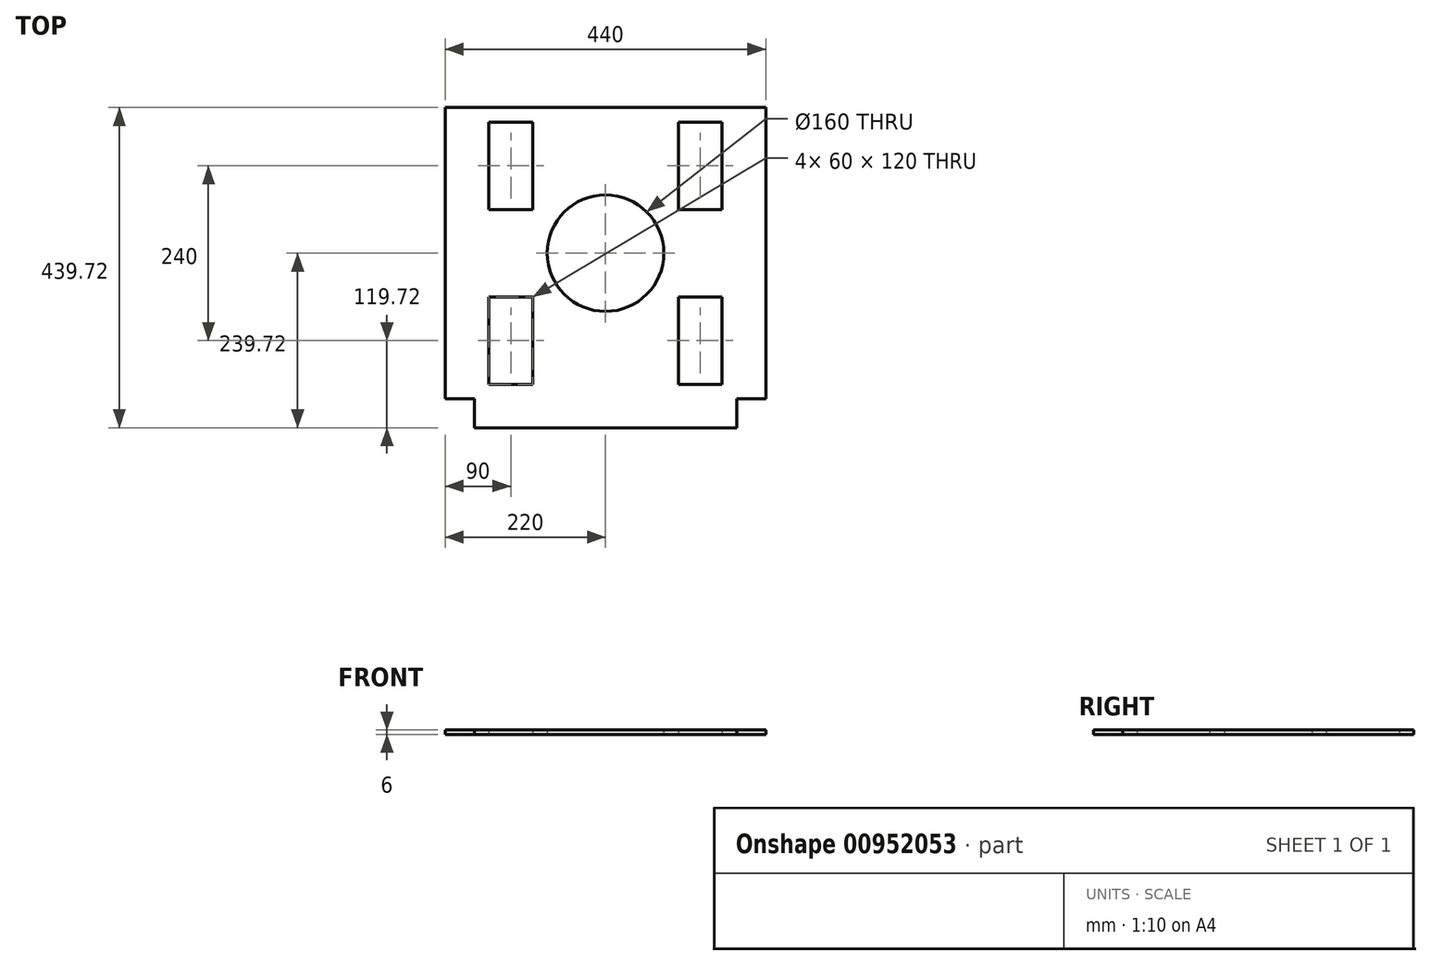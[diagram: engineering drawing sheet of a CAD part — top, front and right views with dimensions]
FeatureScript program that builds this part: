
annotation { "Feature Type Name" : "Feature", "Feature Type Description" : "" }
export const myFeature = defineFeature(function(context is Context, id is Id, definition is map)
    precondition{}
    {
        {
            var Q0;
            Q0=qCreatedBy(makeId("Top.planeOp"),FACE);
            var sketch = newSketch(context, id + "F0", { "sketchPlane" : qUnion([Q0])});
            skLineSegment(sketch, "E0.bottom", {"start": v(180, -200) * mm, "end": v(-180, -200) * mm});
            skLineSegment(sketch, "E0.top", {"start": v(180, 200) * mm, "end": v(-180, 200) * mm});
            skLineSegment(sketch, "E0.left", {"start": v(180, -200) * mm, "end": v(180, 200) * mm});
            skLineSegment(sketch, "E0.right", {"start": v(-180, -200) * mm, "end": v(-180, 200) * mm});
            skPoint(sketch, "E0.middle", {"position": v(0, 0) * mm});
            skLineSegment(sketch, "E1.bottom", {"start": v(-160, 180) * mm, "end": v(-100, 180) * mm});
            skLineSegment(sketch, "E1.top", {"start": v(-160, 60) * mm, "end": v(-100, 60) * mm});
            skLineSegment(sketch, "E1.left", {"start": v(-160, 180) * mm, "end": v(-160, 60) * mm});
            skLineSegment(sketch, "E1.right", {"start": v(-100, 180) * mm, "end": v(-100, 60) * mm});
            skLineSegment(sketch, "E2.MirrorCS", {"start": v(100, 180) * mm, "end": v(100, 60) * mm});
            skLineSegment(sketch, "E3.MirrorCS", {"start": v(160, 180) * mm, "end": v(100, 180) * mm});
            skLineSegment(sketch, "E4.MirrorCS", {"start": v(160, 180) * mm, "end": v(160, 60) * mm});
            skLineSegment(sketch, "E5.MirrorCS", {"start": v(160, 60) * mm, "end": v(100, 60) * mm});
            skLineSegment(sketch, "E6.MirrorCS", {"start": v(-160, -60) * mm, "end": v(-100, -60) * mm});
            skLineSegment(sketch, "E7.MirrorCS", {"start": v(-100, -180) * mm, "end": v(-100, -60) * mm});
            skLineSegment(sketch, "E8.MirrorCS", {"start": v(-160, -180) * mm, "end": v(-160, -60) * mm});
            skLineSegment(sketch, "E9.MirrorCS", {"start": v(-160, -180) * mm, "end": v(-100, -180) * mm});
            skLineSegment(sketch, "E10.MirrorCS", {"start": v(160, -60) * mm, "end": v(100, -60) * mm});
            skLineSegment(sketch, "E11.MirrorCS", {"start": v(100, -180) * mm, "end": v(100, -60) * mm});
            skLineSegment(sketch, "E12.MirrorCS", {"start": v(160, -180) * mm, "end": v(160, -60) * mm});
            skLineSegment(sketch, "E13.MirrorCS", {"start": v(160, -180) * mm, "end": v(100, -180) * mm});
            skLineSegment(sketch, "E14.bottom", {"start": v(-180, 200) * mm, "end": v(180, 200) * mm});
            skLineSegment(sketch, "E14.top", {"start": v(-180, 240) * mm, "end": v(180, 240) * mm});
            skLineSegment(sketch, "E14.left", {"start": v(-180, 200) * mm, "end": v(-180, 240) * mm});
            skLineSegment(sketch, "E14.right", {"start": v(180, 200) * mm, "end": v(180, 240) * mm});
            skLineSegment(sketch, "E15.bottom", {"start": v(180, 200) * mm, "end": v(220, 200) * mm});
            skLineSegment(sketch, "E15.top", {"start": v(180, -199.72) * mm, "end": v(220, -199.72) * mm});
            skLineSegment(sketch, "E15.left", {"start": v(180, 200) * mm, "end": v(180, -199.72) * mm});
            skLineSegment(sketch, "E15.right", {"start": v(220, 200) * mm, "end": v(220, -199.72) * mm});
            skLineSegment(sketch, "E16.bottom", {"start": v(180, -199.72) * mm, "end": v(-180, -199.72) * mm});
            skLineSegment(sketch, "E16.top", {"start": v(180, -239.72) * mm, "end": v(-180, -239.72) * mm});
            skLineSegment(sketch, "E16.left", {"start": v(180, -199.72) * mm, "end": v(180, -239.72) * mm});
            skLineSegment(sketch, "E16.right", {"start": v(-180, -199.72) * mm, "end": v(-180, -239.72) * mm});
            skLineSegment(sketch, "E17.bottom", {"start": v(-180, -199.72) * mm, "end": v(-220, -199.72) * mm});
            skLineSegment(sketch, "E17.top", {"start": v(-180, 200) * mm, "end": v(-220, 200) * mm});
            skLineSegment(sketch, "E17.left", {"start": v(-180, -199.72) * mm, "end": v(-180, 200) * mm});
            skLineSegment(sketch, "E17.right", {"start": v(-220, -199.72) * mm, "end": v(-220, 200) * mm});
            skSolve(sketch);
        }
        {
            var Q0;
            Q0=makeQuery(id+"F0.imprint","IMPRINT",FACE,{"disambiguationData":[TD([[makeQuery(id+"F0.imprint","IMPRINT",EDGE,{"derivedFrom":sQuery(id+"F0.wireOp",EDGE,"E0.bottom")}),-1.0]])]});
            var Q1;
            Q1=makeQuery(id+"F0.imprint","IMPRINT",FACE,{"disambiguationData":[TD([[makeQuery(id+"F0.imprint","IMPRINT",EDGE,{"derivedFrom":sQuery(id+"F0.wireOp",EDGE,"E1.bottom")}),1.0]])]});
            var Q2;
            Q2=makeQuery(id+"F0.imprint","IMPRINT",FACE,{"disambiguationData":[TD([[makeQuery(id+"F0.imprint","IMPRINT",EDGE,{"derivedFrom":sQuery(id+"F0.wireOp",EDGE,"E17.bottom")}),-1.0]])]});
            var Q3;
            Q3=makeQuery(id+"F0.imprint","IMPRINT",FACE,{"disambiguationData":[TD([[makeQuery(id+"F0.imprint","IMPRINT",EDGE,{"derivedFrom":sQuery(id+"F0.wireOp",EDGE,"E14.bottom")}),1.0]])]});
            var Q4;
            {var subQ0=sQuery(id+"F0.wireOp",EDGE,"E0.bottom");Q4=makeQuery(id+"F0.imprint","IMPRINT",FACE,{"disambiguationData":[TD([[makeQuery(id+"F0.imprint","IMPRINT",EDGE,{"derivedFrom":subQ0}),1.0]])]});}
            var Q5;
            Q5=makeQuery(id+"F0.imprint","IMPRINT",FACE,{"disambiguationData":[TD([[makeQuery(id+"F0.imprint","IMPRINT",EDGE,{"derivedFrom":sQuery(id+"F0.wireOp",EDGE,"E15.bottom")}),-1.0]])]});
            extrude(context, id + "F1", {"entities" : qUnion([Q0, Q1, Q2, Q3, Q4, Q5]), "depth" : 6 * mm, "offsetDistance" : 25 * mm});
        }
        {
            var Q0;
            Q0=sQuery(id+"F0.wireOp",VERTEX,"E0.middle");
            var Q1;
            Q1=makeQuery(id+"F1.opExtrude","SWEPT_BODY",BODY,{"disambiguationData":[OSD([sQuery(id+"F0.wireOp",EDGE,"E0.bottom"),sQuery(id+"F0.wireOp",EDGE,"E0.top"),sQuery(id+"F0.wireOp",EDGE,"E0.left"),sQuery(id+"F0.wireOp",EDGE,"E0.right"),sQuery(id+"F0.wireOp",EDGE,"E1.bottom"),sQuery(id+"F0.wireOp",EDGE,"E1.top"),sQuery(id+"F0.wireOp",EDGE,"E1.left"),sQuery(id+"F0.wireOp",EDGE,"E1.right"),sQuery(id+"F0.wireOp",EDGE,"E2.MirrorCS"),sQuery(id+"F0.wireOp",EDGE,"E3.MirrorCS"),sQuery(id+"F0.wireOp",EDGE,"E4.MirrorCS"),sQuery(id+"F0.wireOp",EDGE,"E5.MirrorCS"),sQuery(id+"F0.wireOp",EDGE,"E7.MirrorCS"),sQuery(id+"F0.wireOp",EDGE,"E8.MirrorCS"),sQuery(id+"F0.wireOp",EDGE,"E6.MirrorCS"),sQuery(id+"F0.wireOp",EDGE,"E9.MirrorCS"),sQuery(id+"F0.wireOp",EDGE,"E10.MirrorCS"),sQuery(id+"F0.wireOp",EDGE,"E11.MirrorCS"),sQuery(id+"F0.wireOp",EDGE,"E12.MirrorCS"),sQuery(id+"F0.wireOp",EDGE,"E13.MirrorCS")])]});
            hole(context, id + "F2", {"style" : HoleStyle.SIMPLE, "endStyle" : HoleEndStyle.THROUGH, "oppositeDirection" : true, "holeDiameter" : 160 * mm, "majorDiameter" : 5 * mm, "isTappedThrough" : true, "tappedDepth" : 12 * mm, "tapClearance" : 3, "locations" : qUnion([Q0]), "scope" : qUnion([Q1])});
        }
    });
